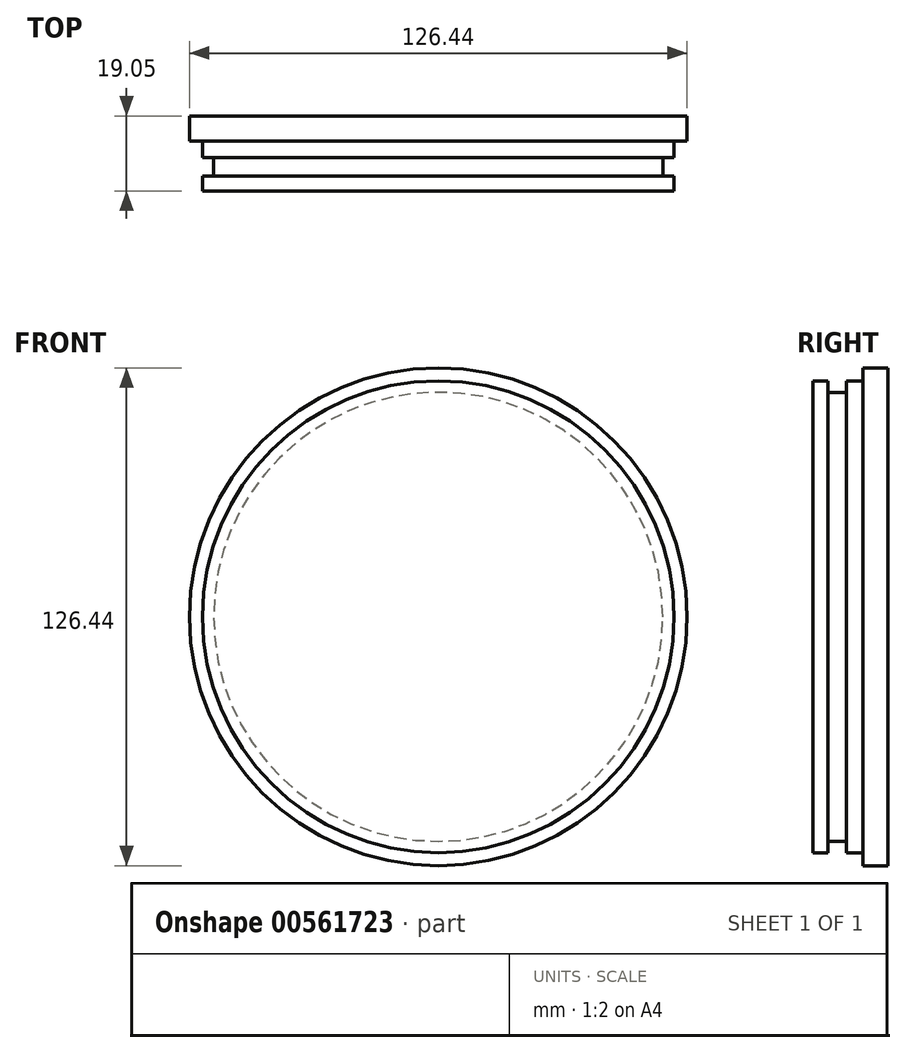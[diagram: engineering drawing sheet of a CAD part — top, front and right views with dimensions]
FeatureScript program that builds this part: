
annotation { "Feature Type Name" : "Feature", "Feature Type Description" : "" }
export const myFeature = defineFeature(function(context is Context, id is Id, definition is map)
    precondition{}
    {
        {
            var Q0;
            Q0=qCreatedBy(makeId("Top.planeOp"),FACE);
            var sketch = newSketch(context, id + "F0", { "sketchPlane" : qUnion([Q0])});
            skLineSegment(sketch, "E0", {"start": v(0, 0) * mm, "end": v(0, 19.05) * mm});
            skLineSegment(sketch, "E1", {"start": v(0, 19.05) * mm, "end": v(63.22, 19.05) * mm});
            skLineSegment(sketch, "E2", {"start": v(0, 0) * mm, "end": v(59.92, 0) * mm});
            skLineSegment(sketch, "E3", {"start": v(59.92, 0) * mm, "end": v(59.92, 12.7) * mm});
            skLineSegment(sketch, "E4", {"start": v(59.92, 12.7) * mm, "end": v(63.22, 12.7) * mm});
            skLineSegment(sketch, "E5", {"start": v(63.22, 12.7) * mm, "end": v(63.22, 19.05) * mm});
            skLineSegment(sketch, "E6", {"start": v(59.92, 3.8) * mm, "end": v(57.05, 3.8) * mm});
            skLineSegment(sketch, "E7", {"start": v(57.05, 3.8) * mm, "end": v(57.05, 8.46) * mm});
            skLineSegment(sketch, "E8", {"start": v(57.05, 8.46) * mm, "end": v(59.92, 8.46) * mm});
            skSolve(sketch);
        }
        {
            var Q0;
            Q0=makeQuery(id+"F0.imprint","IMPRINT",FACE,{"disambiguationData":[TD([[makeQuery(id+"F0.imprint","IMPRINT",EDGE,{"derivedFrom":sQuery(id+"F0.wireOp",EDGE,"E0")}),-1.0]])]});
            var Q1;
            Q1=sQuery(id+"F0.wireOp",EDGE,"E0");
            revolve(context, id + "F1", {"entities" : qUnion([Q0]), "axis" : qUnion([Q1]), "revolveType" : RevolveType.FULL});
        }
    });
